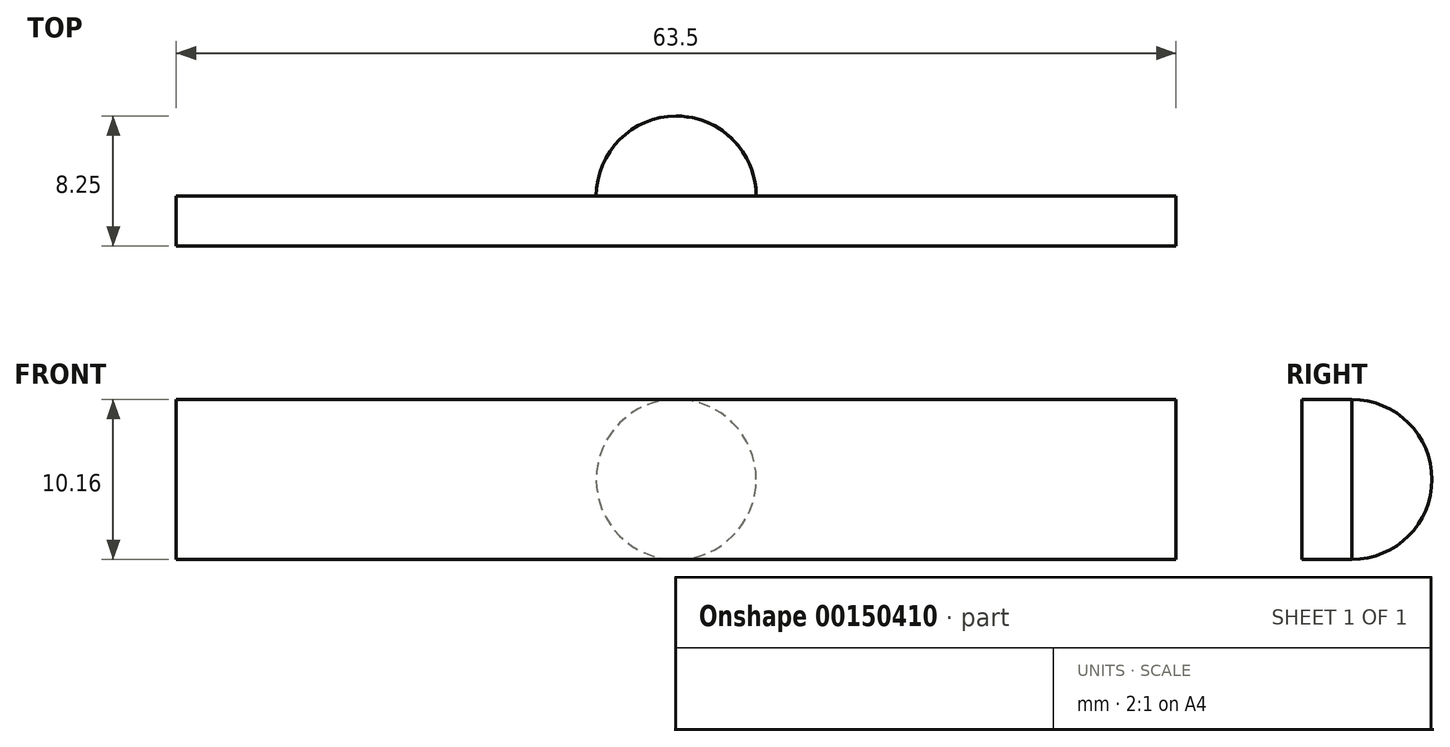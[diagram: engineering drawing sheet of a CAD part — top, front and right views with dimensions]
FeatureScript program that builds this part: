
annotation { "Feature Type Name" : "Feature", "Feature Type Description" : "" }
export const myFeature = defineFeature(function(context is Context, id is Id, definition is map)
    precondition{}
    {
        {
            var Q0;
            Q0=qCreatedBy(makeId("Front.planeOp"),FACE);
            var sketch = newSketch(context, id + "F0", { "sketchPlane" : qUnion([Q0])});
            skLineSegment(sketch, "E0.bottom", {"start": v(31.75, -5.08) * mm, "end": v(-31.75, -5.08) * mm});
            skLineSegment(sketch, "E0.top", {"start": v(31.75, 5.08) * mm, "end": v(-31.75, 5.08) * mm});
            skLineSegment(sketch, "E0.left", {"start": v(31.75, -5.08) * mm, "end": v(31.75, 5.08) * mm});
            skLineSegment(sketch, "E0.right", {"start": v(-31.75, -5.08) * mm, "end": v(-31.75, 5.08) * mm});
            skPoint(sketch, "E0.middle", {"position": v(0, 0) * mm});
            skSolve(sketch);
        }
        {
            var Q0;
            Q0=makeQuery(id+"F0.imprint","IMPRINT",FACE,{"disambiguationData":[TD([[makeQuery(id+"F0.imprint","IMPRINT",EDGE,{"derivedFrom":sQuery(id+"F0.wireOp",EDGE,"E0.bottom")}),-1.0]])]});
            extrude(context, id + "F1", {"entities" : qUnion([Q0]), "depth" : 3.17 * mm});
        }
        {
            var Q0;
            Q0=qCreatedBy(makeId("Top.planeOp"),FACE);
            var sketch = newSketch(context, id + "F2", { "sketchPlane" : qUnion([Q0])});
            skArc(sketch, "E1", {"start": v(5.08, 0) * mm, "mid": v(3.6, 3.6) * mm, "end": v(0, 5.08) * mm});
            skLineSegment(sketch, "E2", {"start": v(5.08, 0) * mm, "end": v(-5.08, 0) * mm});
            skLineSegment(sketch, "E3", {"start": v(0, 0) * mm, "end": v(0, 5.08) * mm});
            skSolve(sketch);
        }
        {
            var Q0;
            {var subQ0=sQuery(id+"F2.wireOp",EDGE,"E1");Q0=makeQuery(id+"F2.imprint","IMPRINT",FACE,{"disambiguationData":[TD([[makeQuery(id+"F2.imprint","IMPRINT",EDGE,{"derivedFrom":subQ0}),1.0]])]});}
            var Q1;
            Q1=sQuery(id+"F2.wireOp",EDGE,"E3");
            revolve(context, id + "F3", {"operationType" : NewBodyOperationType.ADD, "entities" : qUnion([Q0]), "axis" : qUnion([Q1]), "revolveType" : RevolveType.FULL});
        }
    });
